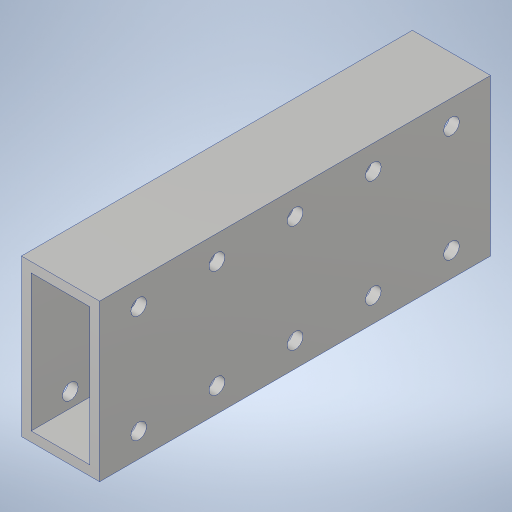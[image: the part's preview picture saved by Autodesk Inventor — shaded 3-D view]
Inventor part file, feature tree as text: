
AUTODESK INVENTOR PART (.ipt)
format: ipt  version: 2023.4 (Build 274418000, 418)  size: 265,216 bytes
history: native  units: in
note: dims shown in document units (in); Inventor stores cm internally (conversion verified against a paired STEP export)
features: extrude x1, hole x1, sketch x1, projected_geometry x1
ambient origin geometry x8: Origin, YZ Plane, XZ Plane, XY Plane, X Axis, Y Axis, Z Axis, Center Point
bodies: Solid1 (feature_tree)
feature tree (4):
  extrude  "Extrusion1"  Depth=1.0in
  hole  "Hole1"  [1 undecoded]
  sketch  "Sketch2"  dims[d4=0.0in d5=0.375in d6=0.375in d7=0.5in d8=3.937in d10=1.0in d11=0.3937in d13=1.0in d15=0.201in d16=0.75in d17=0.385in d18=0.25in d19=0.5635in d20=1.0in d21=0.8108in]
  projected_geometry  "Projected Loop1"
note: 1 required parameter value undecoded (feature->parameter linkage not recoverable at this tier; creation-order binding heuristic only, values carry confidence <= 0.55)
